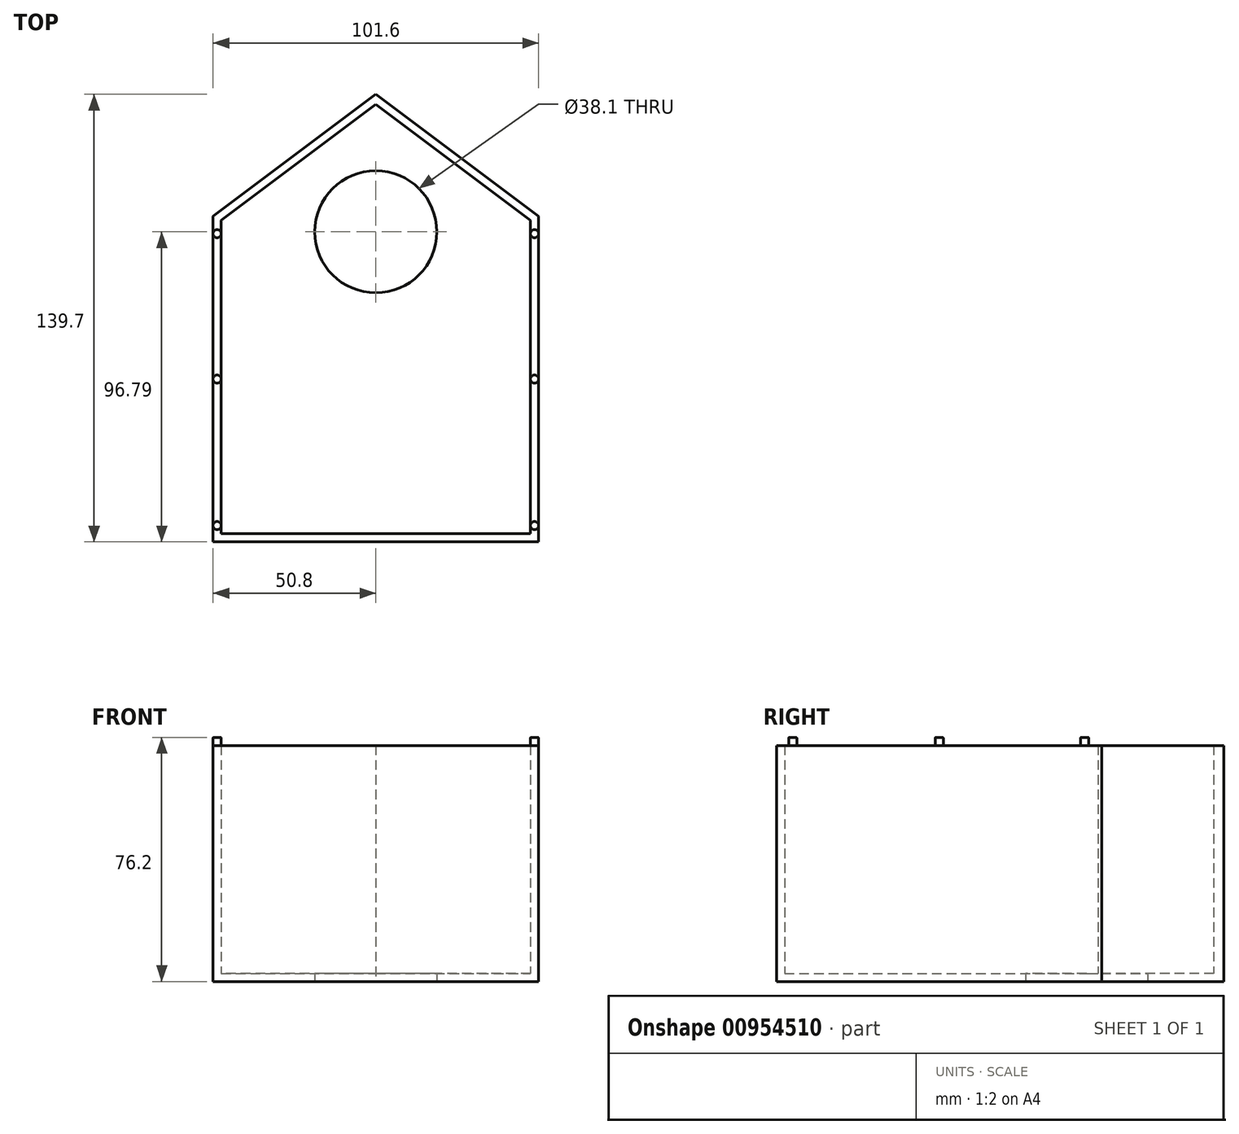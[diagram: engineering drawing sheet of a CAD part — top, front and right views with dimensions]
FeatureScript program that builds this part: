
annotation { "Feature Type Name" : "Feature", "Feature Type Description" : "" }
export const myFeature = defineFeature(function(context is Context, id is Id, definition is map)
    precondition{}
    {
        {
            var Q0;
            Q0=qCreatedBy(makeId("Top.planeOp"),FACE);
            var sketch = newSketch(context, id + "F0", { "sketchPlane" : qUnion([Q0])});
            skLineSegment(sketch, "E0.bottom", {"start": v(50.8, -50.8) * mm, "end": v(-50.8, -50.8) * mm});
            skLineSegment(sketch, "E0.top", {"start": v(50.8, 50.8) * mm, "end": v(-50.8, 50.8) * mm});
            skLineSegment(sketch, "E0.left", {"start": v(50.8, -50.8) * mm, "end": v(50.8, 50.8) * mm});
            skLineSegment(sketch, "E0.right", {"start": v(-50.8, -50.8) * mm, "end": v(-50.8, 50.8) * mm});
            skPoint(sketch, "E0.middle", {"position": v(0, 0) * mm});
            skLineSegment(sketch, "E1", {"start": v(-50.8, 50.8) * mm, "end": v(0, 88.9) * mm});
            skLineSegment(sketch, "E2", {"start": v(0, 88.9) * mm, "end": v(-25.4, 69.85) * mm});
            skLineSegment(sketch, "E3", {"start": v(0, 88.9) * mm, "end": v(50.8, 50.8) * mm});
            skPoint(sketch, "E4", {"position": v(0, 88.9) * mm});
            skSolve(sketch);
        }
        {
            var Q0;
            Q0=makeQuery(id+"F0.imprint","IMPRINT",FACE,{"disambiguationData":[TD([[makeQuery(id+"F0.imprint","IMPRINT",EDGE,{"derivedFrom":sQuery(id+"F0.wireOp",EDGE,"E0.bottom")}),-1.0]])]});
            var Q1;
            Q1=makeQuery(id+"F0.imprint","IMPRINT",FACE,{"disambiguationData":[TD([[makeQuery(id+"F0.imprint","IMPRINT",EDGE,{"derivedFrom":sQuery(id+"F0.wireOp",EDGE,"E0.top")}),-1.0]])]});
            extrude(context, id + "F1", {"entities" : qUnion([Q0, Q1]), "depth" : 73.66 * mm, "offsetDistance" : 25.4 * mm});
        }
        {
            var Q0;
            Q0=makeQuery(id+"F1.opExtrude","CAP_FACE",FACE,{"disambiguationData":[OSD([sQuery(id+"F0.wireOp",EDGE,"E0.bottom"),sQuery(id+"F0.wireOp",EDGE,"E0.left"),sQuery(id+"F0.wireOp",EDGE,"E0.right"),sQuery(id+"F0.wireOp",EDGE,"E1"),sQuery(id+"F0.wireOp",EDGE,"E2"),sQuery(id+"F0.wireOp",EDGE,"E3")])],"isStart":false});
            shell(context, id + "F2", {"entities" : qUnion([Q0]), "thickness" : 2.54 * mm});
        }
        {
            var Q0;
            Q0=makeQuery(id+"F1.opExtrude","CAP_FACE",FACE,{"disambiguationData":[OSD([sQuery(id+"F0.wireOp",EDGE,"E0.bottom"),sQuery(id+"F0.wireOp",EDGE,"E0.left"),sQuery(id+"F0.wireOp",EDGE,"E0.right"),sQuery(id+"F0.wireOp",EDGE,"E1"),sQuery(id+"F0.wireOp",EDGE,"E2"),sQuery(id+"F0.wireOp",EDGE,"E3")])],"isStart":false});
            var sketch = newSketch(context, id + "F3", { "sketchPlane" : qUnion([Q0])});
            skLineSegment(sketch, "E5.bottom", {"start": v(48.26, -8.57) * mm, "end": v(-48.26, -8.57) * mm});
            skLineSegment(sketch, "E5.top", {"start": v(48.26, 8.57) * mm, "end": v(-48.26, 8.57) * mm});
            skLineSegment(sketch, "E5.left", {"start": v(48.26, -8.57) * mm, "end": v(48.26, 8.57) * mm});
            skLineSegment(sketch, "E5.right", {"start": v(-48.26, -8.57) * mm, "end": v(-48.26, 8.57) * mm});
            skPoint(sketch, "E5.middle", {"position": v(0, 0) * mm});
            skSolve(sketch);
        }
        {
            var Q0;
            Q0=qCreatedBy(makeId("Top.planeOp"),FACE);
            var sketch = newSketch(context, id + "F4", { "sketchPlane" : qUnion([Q0])});
            skPoint(sketch, "E6", {"position": v(0, 46) * mm});
            skSolve(sketch);
        }
        {
            var Q0;
            Q0=sQuery(id+"F4.wireOp",VERTEX,"E6");
            var Q1;
            Q1=makeQuery(id+"F1.opExtrude","SWEPT_BODY",BODY,{"disambiguationData":[OSD([sQuery(id+"F0.wireOp",EDGE,"E0.bottom"),sQuery(id+"F0.wireOp",EDGE,"E0.left"),sQuery(id+"F0.wireOp",EDGE,"E0.right"),sQuery(id+"F0.wireOp",EDGE,"E1"),sQuery(id+"F0.wireOp",EDGE,"E2"),sQuery(id+"F0.wireOp",EDGE,"E3")])]});
            hole(context, id + "F5", {"style" : HoleStyle.SIMPLE, "endStyle" : HoleEndStyle.THROUGH, "oppositeDirection" : true, "holeDiameter" : 38.1 * mm, "majorDiameter" : 6.35 * mm, "isTappedThrough" : true, "tappedDepth" : 12.7 * mm, "tapClearance" : 3, "locations" : qUnion([Q0]), "scope" : qUnion([Q1])});
        }
        {
            var Q0;
            Q0=makeQuery(id+"F1.opExtrude","CAP_FACE",FACE,{"disambiguationData":[OSD([sQuery(id+"F0.wireOp",EDGE,"E0.bottom"),sQuery(id+"F0.wireOp",EDGE,"E0.left"),sQuery(id+"F0.wireOp",EDGE,"E0.right"),sQuery(id+"F0.wireOp",EDGE,"E1"),sQuery(id+"F0.wireOp",EDGE,"E2"),sQuery(id+"F0.wireOp",EDGE,"E3")])],"isStart":false});
            var sketch = newSketch(context, id + "F6", { "sketchPlane" : qUnion([Q0])});
            skPoint(sketch, "E7", {"position": v(-49.53, 45.4) * mm});
            skPoint(sketch, "E8", {"position": v(49.53, 45.4) * mm});
            skPoint(sketch, "E9", {"position": v(-49.53, -45.72) * mm});
            skPoint(sketch, "E10", {"position": v(49.53, -45.72) * mm});
            skCircle(sketch, "E11", {"center": v(-49.53, 45.4) * mm, "radius": 1.27 * mm});
            skCircle(sketch, "E12", {"center": v(49.53, 45.4) * mm, "radius": 1.27 * mm});
            skCircle(sketch, "E13", {"center": v(-49.53, -45.72) * mm, "radius": 1.27 * mm});
            skCircle(sketch, "E14", {"center": v(49.53, -45.72) * mm, "radius": 1.27 * mm});
            skPoint(sketch, "E15", {"position": v(-67.24, -6.3) * mm});
            skPoint(sketch, "E16", {"position": v(-49.53, 0) * mm});
            skPoint(sketch, "E17", {"position": v(49.53, 0) * mm});
            skCircle(sketch, "E18", {"center": v(49.53, 0) * mm, "radius": 1.27 * mm});
            skCircle(sketch, "E19", {"center": v(-49.53, 0) * mm, "radius": 1.27 * mm});
            skSolve(sketch);
        }
        {
            var Q0;
            {var subQ0=sQuery(id+"F6.wireOp",EDGE,"E11");var subQ1=sQuery(id+"F0.wireOp",EDGE,"E0.right");var subQ2=makeQuery(id+"F1.opExtrude","CAP_EDGE",EDGE,{"disambiguationData":[OSD([subQ1])],"isStart":false});var subQ3=makeQuery(id+"F6.imprint","INTERSECT",VERTEX,{"derivedFrom":[subQ2,subQ0]});Q0=makeQuery(id+"F6.imprint","IMPRINT",FACE,{"disambiguationData":[TD([[makeQuery(id+"F6.imprint","IMPRINT",EDGE,{"disambiguationData":[TD([[subQ3,1.0]])],"derivedFrom":subQ0}),1.0]])]});}
            var Q1;
            {var subQ0=sQuery(id+"F6.wireOp",EDGE,"E19");var subQ1=sQuery(id+"F0.wireOp",EDGE,"E0.right");var subQ2=makeQuery(id+"F1.opExtrude","CAP_EDGE",EDGE,{"disambiguationData":[OSD([subQ1])],"isStart":false});var subQ3=makeQuery(id+"F6.imprint","INTERSECT",VERTEX,{"derivedFrom":[subQ2,subQ0]});Q1=makeQuery(id+"F6.imprint","IMPRINT",FACE,{"disambiguationData":[TD([[makeQuery(id+"F6.imprint","IMPRINT",EDGE,{"disambiguationData":[TD([[subQ3,1.0]])],"derivedFrom":subQ0}),1.0]])]});}
            var Q2;
            {var subQ0=sQuery(id+"F6.wireOp",EDGE,"E13");var subQ1=sQuery(id+"F0.wireOp",EDGE,"E0.right");var subQ2=makeQuery(id+"F1.opExtrude","CAP_EDGE",EDGE,{"disambiguationData":[OSD([subQ1])],"isStart":false});var subQ3=makeQuery(id+"F6.imprint","INTERSECT",VERTEX,{"derivedFrom":[subQ2,subQ0]});Q2=makeQuery(id+"F6.imprint","IMPRINT",FACE,{"disambiguationData":[TD([[makeQuery(id+"F6.imprint","IMPRINT",EDGE,{"disambiguationData":[TD([[subQ3,1.0]])],"derivedFrom":subQ0}),1.0]])]});}
            var Q3;
            {var subQ0=sQuery(id+"F6.wireOp",EDGE,"E12");var subQ1=sQuery(id+"F0.wireOp",EDGE,"E0.left");var subQ2=makeQuery(id+"F1.opExtrude","CAP_EDGE",EDGE,{"disambiguationData":[OSD([subQ1])],"isStart":false});var subQ3=makeQuery(id+"F6.imprint","INTERSECT",VERTEX,{"derivedFrom":[subQ2,subQ0]});Q3=makeQuery(id+"F6.imprint","IMPRINT",FACE,{"disambiguationData":[TD([[makeQuery(id+"F6.imprint","IMPRINT",EDGE,{"disambiguationData":[TD([[subQ3,-1.0]])],"derivedFrom":subQ0}),1.0]])]});}
            var Q4;
            {var subQ0=sQuery(id+"F6.wireOp",EDGE,"E18");var subQ1=sQuery(id+"F0.wireOp",EDGE,"E0.left");var subQ2=makeQuery(id+"F1.opExtrude","CAP_EDGE",EDGE,{"disambiguationData":[OSD([subQ1])],"isStart":false});var subQ3=makeQuery(id+"F6.imprint","INTERSECT",VERTEX,{"derivedFrom":[subQ2,subQ0]});Q4=makeQuery(id+"F6.imprint","IMPRINT",FACE,{"disambiguationData":[TD([[makeQuery(id+"F6.imprint","IMPRINT",EDGE,{"disambiguationData":[TD([[subQ3,-1.0]])],"derivedFrom":subQ0}),1.0]])]});}
            var Q5;
            {var subQ0=sQuery(id+"F6.wireOp",EDGE,"E14");var subQ1=sQuery(id+"F0.wireOp",EDGE,"E0.left");var subQ2=makeQuery(id+"F1.opExtrude","CAP_EDGE",EDGE,{"disambiguationData":[OSD([subQ1])],"isStart":false});var subQ3=makeQuery(id+"F6.imprint","INTERSECT",VERTEX,{"derivedFrom":[subQ2,subQ0]});Q5=makeQuery(id+"F6.imprint","IMPRINT",FACE,{"disambiguationData":[TD([[makeQuery(id+"F6.imprint","IMPRINT",EDGE,{"disambiguationData":[TD([[subQ3,-1.0]])],"derivedFrom":subQ0}),1.0]])]});}
            extrude(context, id + "F7", {"entities" : qUnion([Q0, Q1, Q2, Q3, Q4, Q5]), "operationType" : NewBodyOperationType.ADD, "depth" : 2.54 * mm, "offsetDistance" : 25.4 * mm});
        }
        {
            var Q0;
            Q0=makeQuery(id+"F7.opExtrude","CAP_EDGE",EDGE,{"disambiguationData":[OSD([sQuery(id+"F6.wireOp",EDGE,"E11")])],"isStart":false});
            var Q1;
            Q1=makeQuery(id+"F7.opExtrude","CAP_EDGE",EDGE,{"disambiguationData":[OSD([sQuery(id+"F6.wireOp",EDGE,"E12")])],"isStart":false});
            var Q2;
            Q2=makeQuery(id+"F7.opExtrude","CAP_EDGE",EDGE,{"disambiguationData":[OSD([sQuery(id+"F6.wireOp",EDGE,"E14")])],"isStart":false});
            var Q3;
            Q3=makeQuery(id+"F7.opExtrude","CAP_EDGE",EDGE,{"disambiguationData":[OSD([sQuery(id+"F6.wireOp",EDGE,"E19")])],"isStart":false});
            var Q4;
            Q4=makeQuery(id+"F7.opExtrude","CAP_EDGE",EDGE,{"disambiguationData":[OSD([sQuery(id+"F6.wireOp",EDGE,"E13")])],"isStart":false});
            var Q5;
            Q5=makeQuery(id+"F7.opExtrude","CAP_EDGE",EDGE,{"disambiguationData":[OSD([sQuery(id+"F6.wireOp",EDGE,"E18")])],"isStart":false});
            fillet(context, id + "F8", {"entities" : qUnion([Q0, Q1, Q2, Q3, Q4, Q5]), "radius" : 0.23 * mm, "tangentPropagation" : true, "allowEdgeOverflow" : false});
        }
    });
